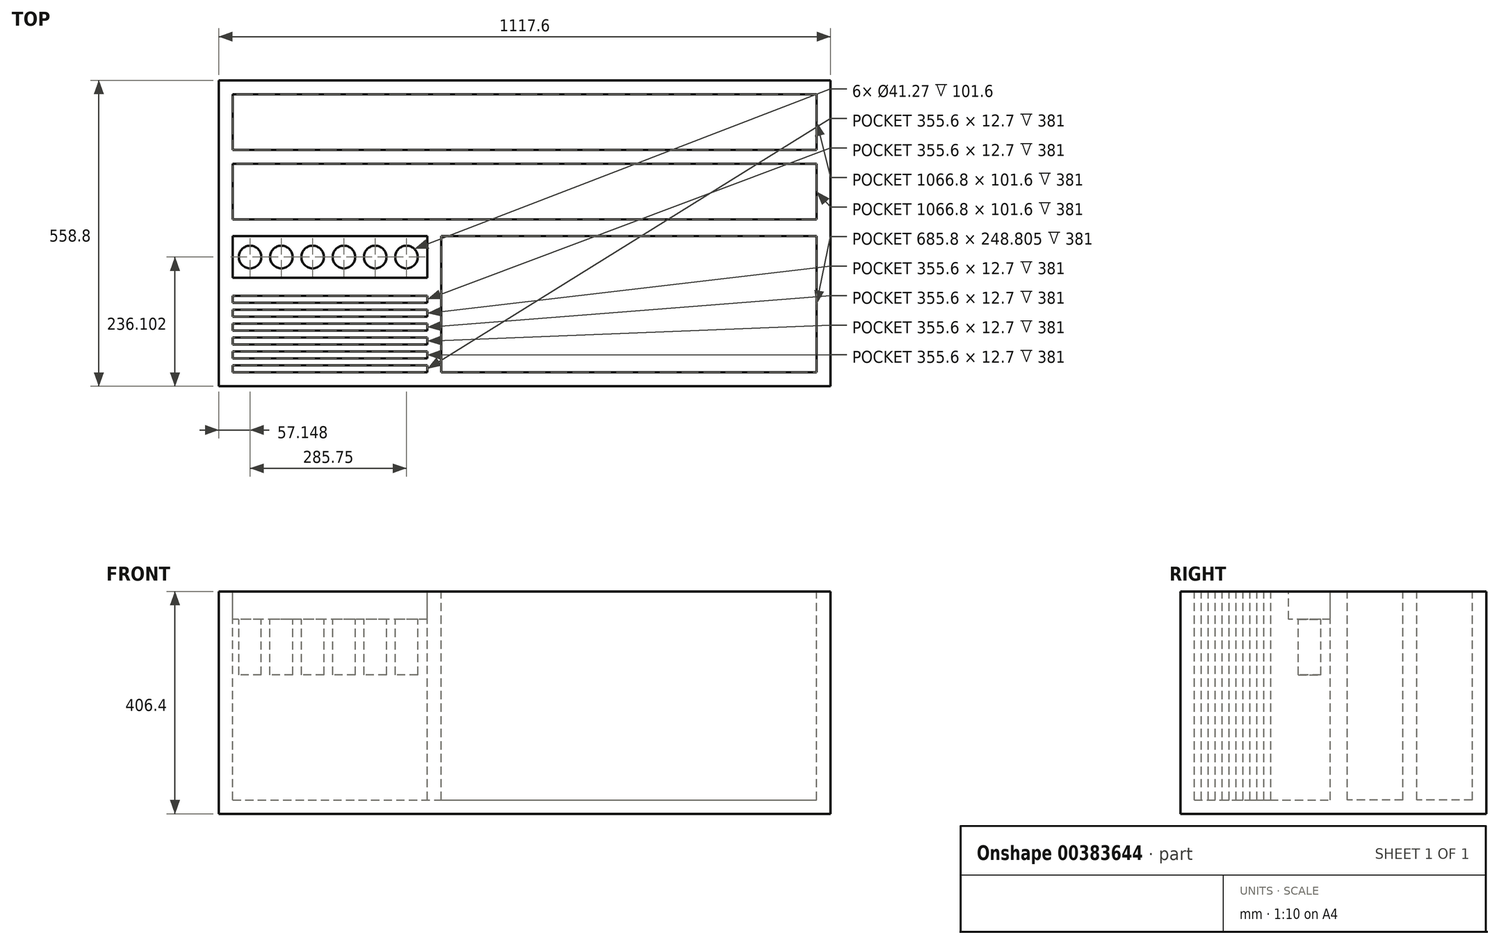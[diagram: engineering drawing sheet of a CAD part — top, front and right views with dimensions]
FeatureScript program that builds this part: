
annotation { "Feature Type Name" : "Feature", "Feature Type Description" : "" }
export const myFeature = defineFeature(function(context is Context, id is Id, definition is map)
    precondition{}
    {
        {
            var Q0;
            Q0=qCreatedBy(makeId("Top.planeOp"),FACE);
            var sketch = newSketch(context, id + "F0", { "sketchPlane" : qUnion([Q0])});
            skLineSegment(sketch, "E0.bottom", {"start": v(-92.78, -48.13) * mm, "end": v(1024.82, -48.13) * mm});
            skLineSegment(sketch, "E0.top", {"start": v(-92.78, 510.67) * mm, "end": v(1024.82, 510.67) * mm});
            skLineSegment(sketch, "E0.left", {"start": v(-92.78, -48.13) * mm, "end": v(-92.78, 510.67) * mm});
            skLineSegment(sketch, "E0.right", {"start": v(1024.82, -48.13) * mm, "end": v(1024.82, 510.67) * mm});
            skSolve(sketch);
        }
        {
            var Q0;
            Q0 = qSketchRegion(id + "F0", true);
            extrude(context, id + "F1", {"entities" : qUnion([Q0]), "depth" : 406.4 * mm});
        }
        {
            var Q0;
            Q0=makeQuery(id+"F1.opExtrude","CAP_FACE",FACE,{"disambiguationData":[OSD([sQuery(id+"F0.wireOp",EDGE,"E0.bottom"),sQuery(id+"F0.wireOp",EDGE,"E0.top"),sQuery(id+"F0.wireOp",EDGE,"E0.left"),sQuery(id+"F0.wireOp",EDGE,"E0.right")])],"isStart":false});
            var sketch = newSketch(context, id + "F2", { "sketchPlane" : qUnion([Q0])});
            skLineSegment(sketch, "E1.bottom", {"start": v(-67.38, -22.73) * mm, "end": v(288.22, -22.73) * mm});
            skLineSegment(sketch, "E1.top", {"start": v(-67.38, -10.03) * mm, "end": v(288.22, -10.03) * mm});
            skLineSegment(sketch, "E1.left", {"start": v(-67.38, -22.73) * mm, "end": v(-67.38, -10.03) * mm});
            skLineSegment(sketch, "E1.right", {"start": v(288.22, -22.73) * mm, "end": v(288.22, -10.03) * mm});
            skLineSegment(sketch, "E2.0.1.0", {"start": v(-67.38, 15.37) * mm, "end": v(288.22, 15.37) * mm});
            skLineSegment(sketch, "E2.0.1.1", {"start": v(-67.38, 2.67) * mm, "end": v(288.22, 2.67) * mm});
            skLineSegment(sketch, "E2.0.1.2", {"start": v(288.22, 2.67) * mm, "end": v(288.22, 15.37) * mm});
            skLineSegment(sketch, "E2.0.1.3", {"start": v(-67.38, 2.67) * mm, "end": v(-67.38, 15.37) * mm});
            skLineSegment(sketch, "E2.0.2.0", {"start": v(-67.38, 40.77) * mm, "end": v(288.22, 40.77) * mm});
            skLineSegment(sketch, "E2.0.2.1", {"start": v(-67.38, 28.07) * mm, "end": v(288.22, 28.07) * mm});
            skLineSegment(sketch, "E2.0.2.2", {"start": v(288.22, 28.07) * mm, "end": v(288.22, 40.77) * mm});
            skLineSegment(sketch, "E2.0.2.3", {"start": v(-67.38, 28.07) * mm, "end": v(-67.38, 40.77) * mm});
            skLineSegment(sketch, "E2.0.3.0", {"start": v(-67.38, 66.17) * mm, "end": v(288.22, 66.17) * mm});
            skLineSegment(sketch, "E2.0.3.1", {"start": v(-67.38, 53.47) * mm, "end": v(288.22, 53.47) * mm});
            skLineSegment(sketch, "E2.0.3.2", {"start": v(288.22, 53.47) * mm, "end": v(288.22, 66.17) * mm});
            skLineSegment(sketch, "E2.0.3.3", {"start": v(-67.38, 53.47) * mm, "end": v(-67.38, 66.17) * mm});
            skLineSegment(sketch, "E2.0.4.0", {"start": v(-67.38, 91.57) * mm, "end": v(288.22, 91.57) * mm});
            skLineSegment(sketch, "E2.0.4.1", {"start": v(-67.38, 78.87) * mm, "end": v(288.22, 78.87) * mm});
            skLineSegment(sketch, "E2.0.4.2", {"start": v(288.22, 78.87) * mm, "end": v(288.22, 91.57) * mm});
            skLineSegment(sketch, "E2.0.4.3", {"start": v(-67.38, 78.87) * mm, "end": v(-67.38, 91.57) * mm});
            skLineSegment(sketch, "E2.0.5.0", {"start": v(-67.38, 116.97) * mm, "end": v(288.22, 116.97) * mm});
            skLineSegment(sketch, "E2.0.5.1", {"start": v(-67.38, 104.27) * mm, "end": v(288.22, 104.27) * mm});
            skLineSegment(sketch, "E2.0.5.2", {"start": v(288.22, 104.27) * mm, "end": v(288.22, 116.97) * mm});
            skLineSegment(sketch, "E2.0.5.3", {"start": v(-67.38, 104.27) * mm, "end": v(-67.38, 116.97) * mm});
            skLineSegment(sketch, "E2.direction1", {"start": v(-67.38, -22.73) * mm, "end": v(-41.98, -22.73) * mm, "construction": true});
            skLineSegment(sketch, "E2.direction2", {"start": v(-67.38, -22.73) * mm, "end": v(-67.38, 2.67) * mm, "construction": true});
            skLineSegment(sketch, "E3.bottom", {"start": v(-67.38, 485.27) * mm, "end": v(999.42, 485.27) * mm});
            skLineSegment(sketch, "E3.top", {"start": v(-67.38, 383.67) * mm, "end": v(999.42, 383.67) * mm});
            skLineSegment(sketch, "E3.left", {"start": v(-67.38, 485.27) * mm, "end": v(-67.38, 383.67) * mm});
            skLineSegment(sketch, "E3.right", {"start": v(999.42, 485.27) * mm, "end": v(999.42, 383.67) * mm});
            skLineSegment(sketch, "E4.0.1.0", {"start": v(-67.38, 358.27) * mm, "end": v(-67.38, 256.67) * mm});
            skLineSegment(sketch, "E4.0.1.1", {"start": v(-67.38, 358.27) * mm, "end": v(999.42, 358.27) * mm});
            skLineSegment(sketch, "E4.0.1.2", {"start": v(-67.38, 256.67) * mm, "end": v(999.42, 256.67) * mm});
            skLineSegment(sketch, "E4.0.1.3", {"start": v(999.42, 358.27) * mm, "end": v(999.42, 256.67) * mm});
            skLineSegment(sketch, "E4.direction1", {"start": v(-67.38, 383.67) * mm, "end": v(-41.98, 383.67) * mm, "construction": true});
            skLineSegment(sketch, "E4.direction2", {"start": v(-67.38, 383.67) * mm, "end": v(-67.38, 256.67) * mm, "construction": true});
            skLineSegment(sketch, "E5.bottom", {"start": v(313.62, -22.73) * mm, "end": v(999.42, -22.73) * mm});
            skLineSegment(sketch, "E5.top", {"start": v(313.62, 226.07) * mm, "end": v(999.42, 226.07) * mm});
            skLineSegment(sketch, "E5.left", {"start": v(313.62, -22.73) * mm, "end": v(313.62, 226.07) * mm});
            skLineSegment(sketch, "E5.right", {"start": v(999.42, -22.73) * mm, "end": v(999.42, 226.07) * mm});
            skSolve(sketch);
        }
        {
            var Q0;
            Q0 = qSketchRegion(id + "F2", true);
            extrude(context, id + "F3", {"entities" : qUnion([Q0]), "operationType" : NewBodyOperationType.REMOVE, "oppositeDirection" : true, "depth" : 381 * mm});
        }
        {
            var Q0;
            Q0=makeQuery(id+"F1.opExtrude","CAP_FACE",FACE,{"disambiguationData":[OSD([sQuery(id+"F0.wireOp",EDGE,"E0.bottom"),sQuery(id+"F0.wireOp",EDGE,"E0.top"),sQuery(id+"F0.wireOp",EDGE,"E0.left"),sQuery(id+"F0.wireOp",EDGE,"E0.right")])],"isStart":false});
            var sketch = newSketch(context, id + "F4", { "sketchPlane" : qUnion([Q0])});
            skLineSegment(sketch, "E6.bottom", {"start": v(288.22, 226.07) * mm, "end": v(-67.38, 226.07) * mm});
            skLineSegment(sketch, "E6.top", {"start": v(288.22, 149.87) * mm, "end": v(-67.38, 149.87) * mm});
            skLineSegment(sketch, "E6.left", {"start": v(288.22, 226.07) * mm, "end": v(288.22, 149.87) * mm});
            skLineSegment(sketch, "E6.right", {"start": v(-67.38, 226.07) * mm, "end": v(-67.38, 149.87) * mm});
            skSolve(sketch);
        }
        {
            var Q0;
            Q0 = qSketchRegion(id + "F4", true);
            extrude(context, id + "F5", {"entities" : qUnion([Q0]), "operationType" : NewBodyOperationType.REMOVE, "oppositeDirection" : true, "depth" : 50.8 * mm});
        }
        {
            var Q0;
            Q0=makeQuery(id+"F5.boolean.opBoolean","COPY",FACE,{"derivedFrom":makeQuery(id+"F5.opExtrude","CAP_FACE",FACE,{"disambiguationData":[OSD([sQuery(id+"F4.wireOp",EDGE,"E6.bottom"),sQuery(id+"F4.wireOp",EDGE,"E6.top"),sQuery(id+"F4.wireOp",EDGE,"E6.left"),sQuery(id+"F4.wireOp",EDGE,"E6.right")])],"isStart":false})});
            var sketch = newSketch(context, id + "F6", { "sketchPlane" : qUnion([Q0])});
            skLineSegment(sketch, "E7", {"start": v(-67.38, 187.97) * mm, "end": v(288.22, 187.97) * mm, "construction": true});
            skCircle(sketch, "E8", {"center": v(-35.63, 187.97) * mm, "radius": 20.64 * mm});
            skCircle(sketch, "E9.1.0.0", {"center": v(21.52, 187.97) * mm, "radius": 20.64 * mm});
            skCircle(sketch, "E9.2.0.0", {"center": v(78.67, 187.97) * mm, "radius": 20.64 * mm});
            skCircle(sketch, "E9.3.0.0", {"center": v(135.82, 187.97) * mm, "radius": 20.64 * mm});
            skCircle(sketch, "E9.4.0.0", {"center": v(192.97, 187.97) * mm, "radius": 20.64 * mm});
            skCircle(sketch, "E9.5.0.0", {"center": v(250.12, 187.97) * mm, "radius": 20.64 * mm});
            skLineSegment(sketch, "E9.direction1", {"start": v(-35.63, 187.97) * mm, "end": v(21.52, 187.97) * mm, "construction": true});
            skSolve(sketch);
        }
        {
            var Q0;
            Q0 = qSketchRegion(id + "F6", true);
            extrude(context, id + "F7", {"entities" : qUnion([Q0]), "operationType" : NewBodyOperationType.REMOVE, "oppositeDirection" : true, "depth" : 101.6 * mm});
        }
    });
